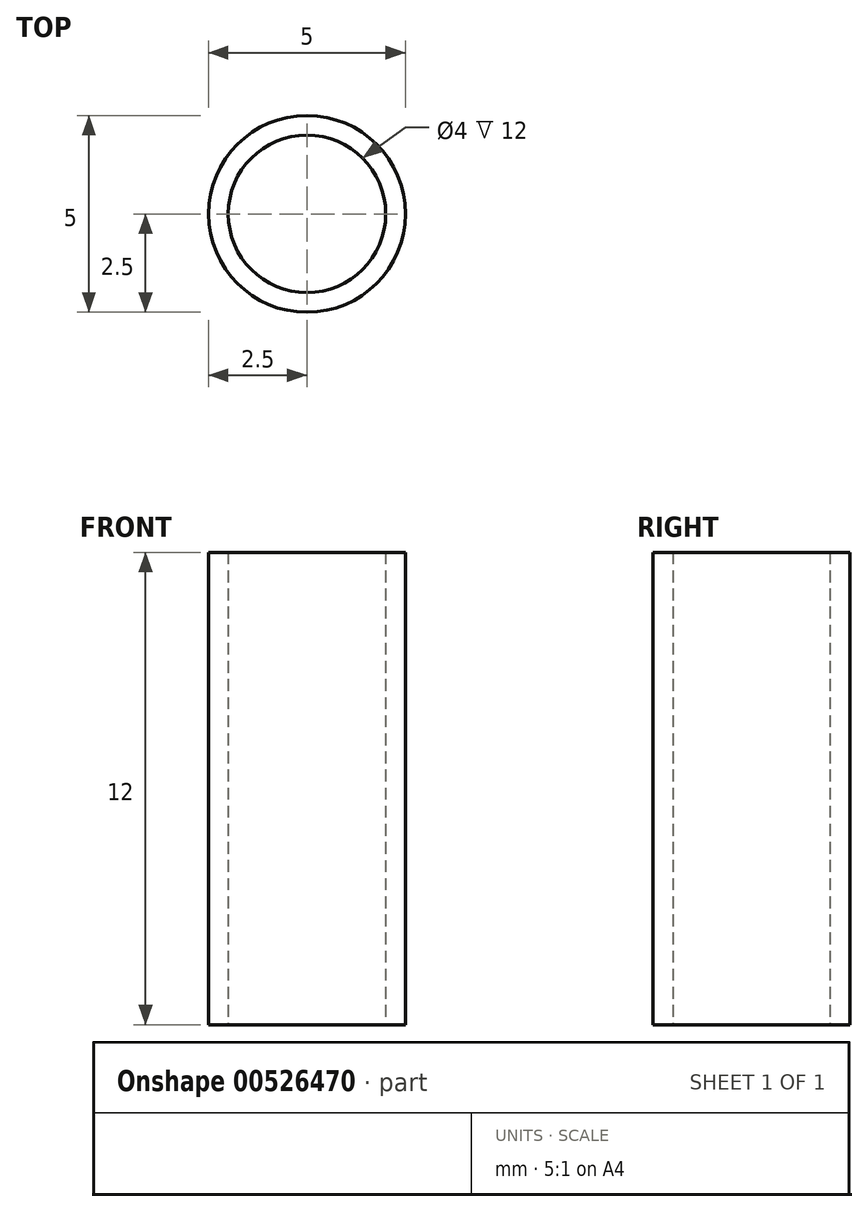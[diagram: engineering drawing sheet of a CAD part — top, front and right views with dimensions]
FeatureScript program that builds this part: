
annotation { "Feature Type Name" : "Feature", "Feature Type Description" : "" }
export const myFeature = defineFeature(function(context is Context, id is Id, definition is map)
    precondition{}
    {
        {
            var Q0;
            Q0=qCreatedBy(makeId("Top.planeOp"),FACE);
            var sketch = newSketch(context, id + "F0", { "sketchPlane" : qUnion([Q0])});
            skCircle(sketch, "E0", {"center": v(0, 0) * mm, "radius": 2 * mm});
            skCircle(sketch, "E1", {"center": v(0, 0) * mm, "radius": 2.5 * mm});
            skSolve(sketch);
        }
        {
            var Q0;
            Q0 = qSketchRegion(id + "F0", true);
            extrude(context, id + "F1", {"entities" : qUnion([Q0]), "depth" : 12 * mm, "offsetDistance" : 25 * mm});
        }
    });
